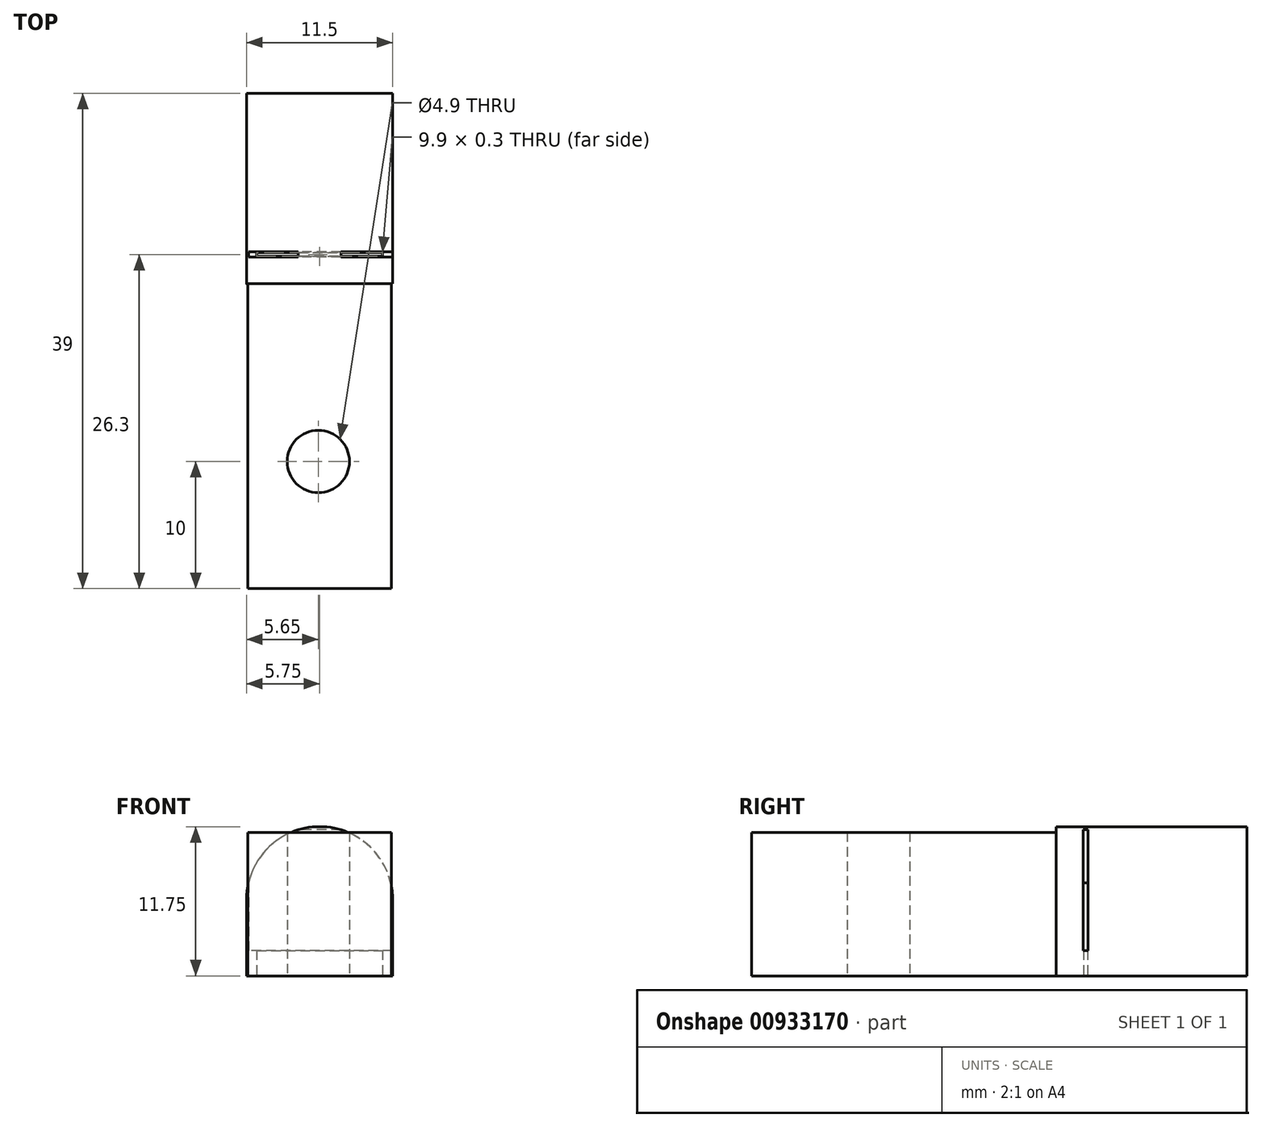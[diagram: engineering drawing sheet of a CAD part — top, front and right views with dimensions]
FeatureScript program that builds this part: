
annotation { "Feature Type Name" : "Feature", "Feature Type Description" : "" }
export const myFeature = defineFeature(function(context is Context, id is Id, definition is map)
    precondition{}
    {
        {
            var Q0;
            Q0=qCreatedBy(makeId("Front.planeOp"),FACE);
            var sketch = newSketch(context, id + "F0", { "sketchPlane" : qUnion([Q0])});
            skLineSegment(sketch, "E0.bottom", {"start": v(0, 0) * mm, "end": v(11.5, 0) * mm});
            skLineSegment(sketch, "E0.top", {"start": v(0, 6) * mm, "end": v(11.5, 6) * mm});
            skLineSegment(sketch, "E0.left", {"start": v(0, 0) * mm, "end": v(0, 6) * mm});
            skLineSegment(sketch, "E0.right", {"start": v(11.5, 0) * mm, "end": v(11.5, 6) * mm});
            skArc(sketch, "E1", {"start": v(0, 6) * mm, "mid": v(5.75, 11.75) * mm, "end": v(11.5, 6) * mm});
            skSolve(sketch);
        }
        {
            var Q0;
            Q0=makeQuery(id+"F0.imprint","IMPRINT",FACE,{"disambiguationData":[TD([[makeQuery(id+"F0.imprint","IMPRINT",EDGE,{"derivedFrom":sQuery(id+"F0.wireOp",EDGE,"E0.top")}),1.0]])]});
            var Q1;
            Q1=makeQuery(id+"F0.imprint","IMPRINT",FACE,{"disambiguationData":[TD([[makeQuery(id+"F0.imprint","IMPRINT",EDGE,{"derivedFrom":sQuery(id+"F0.wireOp",EDGE,"E0.bottom")}),1.0]])]});
            extrude(context, id + "F1", {"entities" : qUnion([Q0, Q1]), "depth" : 15 * mm, "offsetDistance" : 25 * mm});
        }
        {
            var Q0;
            Q0=makeQuery(id+"F1.opExtrude","CAP_FACE",FACE,{"disambiguationData":[OSD([sQuery(id+"F0.wireOp",EDGE,"E0.bottom"),sQuery(id+"F0.wireOp",EDGE,"E0.left"),sQuery(id+"F0.wireOp",EDGE,"E0.right"),sQuery(id+"F0.wireOp",EDGE,"E1")])],"isStart":false});
            var sketch = newSketch(context, id + "F2", { "sketchPlane" : qUnion([Q0])});
            skLineSegment(sketch, "E2.bottom", {"start": v(11.4, 0) * mm, "end": v(0.1, 0) * mm});
            skLineSegment(sketch, "E2.top", {"start": v(11.4, 11.3) * mm, "end": v(0.1, 11.3) * mm});
            skLineSegment(sketch, "E2.left", {"start": v(11.4, 0) * mm, "end": v(11.4, 11.3) * mm});
            skLineSegment(sketch, "E2.right", {"start": v(0.1, 0) * mm, "end": v(0.1, 11.3) * mm});
            skPoint(sketch, "E2.middle", {"position": v(5.75, 5.65) * mm});
            skPoint(sketch, "E2.middle.positionSnap0", {"position": v(5.75, 0) * mm});
            skPoint(sketch, "E2.centerSnap0", {"position": v(5.75, 0) * mm});
            skSolve(sketch);
        }
        {
            var Q0;
            Q0 = qSketchRegion(id + "F2", true);
            extrude(context, id + "F3", {"entities" : qUnion([Q0]), "operationType" : NewBodyOperationType.ADD, "depth" : 24 * mm, "offsetDistance" : 25 * mm});
        }
        {
            var Q0;
            Q0=makeQuery(id+"F1.opExtrude","CAP_VERTEX",VERTEX,{"disambiguationData":[OSD([sQuery(id+"F0.wireOp",EDGE,"E0.top"),sQuery(id+"F0.wireOp",EDGE,"E0.left"),sQuery(id+"F0.wireOp",EDGE,"E1")])],"isStart":true});
            var Q1;
            Q1=makeQuery(id+"F1.opExtrude","CAP_VERTEX",VERTEX,{"disambiguationData":[OSD([sQuery(id+"F0.wireOp",EDGE,"E0.top"),sQuery(id+"F0.wireOp",EDGE,"E0.left"),sQuery(id+"F0.wireOp",EDGE,"E1")])],"isStart":false});
            var Q2;
            Q2=makeQuery(id+"F1.opExtrude","CAP_VERTEX",VERTEX,{"disambiguationData":[OSD([sQuery(id+"F0.wireOp",EDGE,"E0.top"),sQuery(id+"F0.wireOp",EDGE,"E0.right"),sQuery(id+"F0.wireOp",EDGE,"E1")])],"isStart":true});
            cPlane(context, id + "F4", {"entities" : qUnion([Q0, Q1, Q2]), "cplaneType" : CPlaneType.THREE_POINT, "offset" : 25 * mm, "width" : 150 * mm, "height" : 150 * mm});
        }
        {
            var Q0;
            Q0=qCreatedBy(id+"F4.planeOp",FACE);
            var sketch = newSketch(context, id + "F5", { "sketchPlane" : qUnion([Q0])});
            skPoint(sketch, "E3.0", {"position": v(11.9, 12.7) * mm});
            skPoint(sketch, "E4.0", {"position": v(0, 9.7) * mm});
            skLineSegment(sketch, "E5", {"start": v(13.51, 12.7) * mm, "end": v(-0.54, 12.7) * mm, "construction": true});
            skLineSegment(sketch, "E6.bottom", {"start": v(12.82, 12.9) * mm, "end": v(0.15, 12.9) * mm});
            skLineSegment(sketch, "E6.top", {"start": v(12.82, 12.5) * mm, "end": v(0.15, 12.5) * mm});
            skLineSegment(sketch, "E6.left", {"start": v(12.82, 12.9) * mm, "end": v(12.82, 12.5) * mm});
            skLineSegment(sketch, "E6.right", {"start": v(0.15, 12.9) * mm, "end": v(0.15, 12.5) * mm});
            skPoint(sketch, "E6.middle", {"position": v(6.49, 12.7) * mm});
            skSolve(sketch);
        }
        {
            var Q0;
            Q0=makeQuery(id+"F5.imprint","IMPRINT",FACE,{"disambiguationData":[TD([[makeQuery(id+"F5.imprint","IMPRINT",EDGE,{"derivedFrom":sQuery(id+"F5.wireOp",EDGE,"E6.bottom")}),1.0]])]});
            extrude(context, id + "F6", {"entities" : qUnion([Q0]), "operationType" : NewBodyOperationType.REMOVE, "oppositeDirection" : true, "depth" : 5.5 * mm, "offsetDistance" : 25 * mm});
        }
        {
            var Q0;
            Q0=makeQuery(id+"F3.boolean.opBoolean","MERGE",FACE,{"derivedFrom":[makeQuery(id+"F1.opExtrude","SWEPT_FACE",FACE,{"disambiguationData":[OSD([sQuery(id+"F0.wireOp",EDGE,"E0.bottom")])]}),makeQuery(id+"F3.opExtrude","SWEPT_FACE",FACE,{"disambiguationData":[OSD([sQuery(id+"F2.wireOp",EDGE,"E2.bottom")])]})]});
            var sketch = newSketch(context, id + "F7", { "sketchPlane" : qUnion([Q0])});
            skLineSegment(sketch, "E7", {"start": v(11.5, 12.7) * mm, "end": v(0, 12.7) * mm, "construction": true});
            skPoint(sketch, "E8", {"position": v(5.75, 12.7) * mm});
            skLineSegment(sketch, "E9.bottom", {"start": v(10.7, 12.55) * mm, "end": v(0.8, 12.55) * mm});
            skLineSegment(sketch, "E9.top", {"start": v(10.7, 12.85) * mm, "end": v(0.8, 12.85) * mm});
            skLineSegment(sketch, "E9.left", {"start": v(10.7, 12.55) * mm, "end": v(10.7, 12.85) * mm});
            skLineSegment(sketch, "E9.right", {"start": v(0.8, 12.55) * mm, "end": v(0.8, 12.85) * mm});
            skPoint(sketch, "E10", {"position": v(5.65, 29) * mm});
            skPoint(sketch, "E10.positionSnap0", {"position": v(5.65, 15) * mm});
            skSolve(sketch);
        }
        {
            var Q0;
            Q0=makeQuery(id+"F7.imprint","IMPRINT",FACE,{"disambiguationData":[TD([[makeQuery(id+"F7.imprint","IMPRINT",EDGE,{"derivedFrom":sQuery(id+"F7.wireOp",EDGE,"E9.bottom")}),-1.0]])]});
            var Q1;
            Q1=makeQuery(id+"F6.boolean.opBoolean","COPY",FACE,{"derivedFrom":makeQuery(id+"F6.opExtrude","CAP_FACE",FACE,{"disambiguationData":[OSD([sQuery(id+"F5.wireOp",EDGE,"E6.bottom"),sQuery(id+"F5.wireOp",EDGE,"E6.top"),sQuery(id+"F5.wireOp",EDGE,"E6.left"),sQuery(id+"F5.wireOp",EDGE,"E6.right")])],"isStart":true})});
            extrude(context, id + "F8", {"entities" : qUnion([Q0]), "operationType" : NewBodyOperationType.REMOVE, "endBound" : BoundingType.UP_TO_SURFACE, "oppositeDirection" : true, "depth" : 25 * mm, "endBoundEntityFace" : qUnion([Q1]), "offsetDistance" : 25 * mm});
        }
        {
            var Q0;
            Q0=sQuery(id+"F7.wireOp",VERTEX,"E10");
            var Q1;
            Q1=makeQuery(id+"F1.opExtrude","SWEPT_BODY",BODY,{"disambiguationData":[OSD([sQuery(id+"F0.wireOp",EDGE,"E0.bottom"),sQuery(id+"F0.wireOp",EDGE,"E0.left"),sQuery(id+"F0.wireOp",EDGE,"E0.right"),sQuery(id+"F0.wireOp",EDGE,"E1")])]});
            hole(context, id + "F9", {"style" : HoleStyle.SIMPLE, "endStyle" : HoleEndStyle.THROUGH, "holeDiameter" : 4.9 * mm, "majorDiameter" : 5 * mm, "isTappedThrough" : true, "tappedDepth" : 12 * mm, "tapClearance" : 3, "locations" : qUnion([Q0]), "scope" : qUnion([Q1])});
        }
        {
            var Q0;
            Q0 = qSketchRegion(id + "F5", true);
            extrude(context, id + "F10", {"entities" : qUnion([Q0]), "operationType" : NewBodyOperationType.REMOVE, "depth" : 4 * mm, "offsetDistance" : 25 * mm});
        }
    });
